# Revit family: s711_f450_built_in_sink_450_43301807
name_source: partatom
category: Plumbing Fixtures
revit_build: Autodesk Revit 2015 (Build: 20140903_1530(x64)
units: mm (PartAtom-declared; Revit-internal decimal feet)

## types (1)
- Stainless Steel
    BIMobject category = Sinks
    BOSUseNativeGeometries = 1
    Brand url = http://www.hansgrohe-int.com
    Default Elevation = 4' - 0"
    Design country = Germany
    EAN code = https://4011097823560
    Edition number = 1
    IFC Classification = Flow Terminal
    Installation instructions = https://pro.hansgrohe-int.com
    Manufacturer country = Germany
    Manufacturer name = hansgrohe
    Masterformat 2014 Code = 22 41 16.16
    Masterformat 2014 Description = Residential Sinks
    Material main = Stainless steel
    NBS Reference Code = 31-79
    NBS Reference Description = Sinks, Wash Basins And Troughs
    Nominal height = 0
    Nominal width = 0
    OmniClass Code = 23-31 13 00
    OmniClass Description = Sinks
    Product Guid = 91408c70-ded7-428c-9930-38207d1ab843
    Product SKU = 43301807
    Product data url = https://bimobject.com
    Product family = S71
    Product group = Sinks
    Product url = https://pro.hansgrohe-int.com
    QR code = http://bimobject.com
    Technical description = https://pro.hansgrohe-int.com
    UNSPSC Code = 30181504
    Uniclass 1.4 Code = L7232
    Uniclass 1.4 Description = Sinks for kitchens, bars
    Uniclass 2.0 Code = PR-31-79
    Uniclass 2.0 Description = Sinks, Wash Basins And Troughs
    Uniclass 2015 Code = Pr_40_20_96_45
    Uniclass 2015 Name = Kitchen sinks
    Uniformat II Code = D2010
    Uniformat II Description = Plumbing Fixtures
    Weight Net (Kg) = 0

## geometry (parser evidence)
native form markers: Sweep x2
no freeform markers — native parametric forms only
